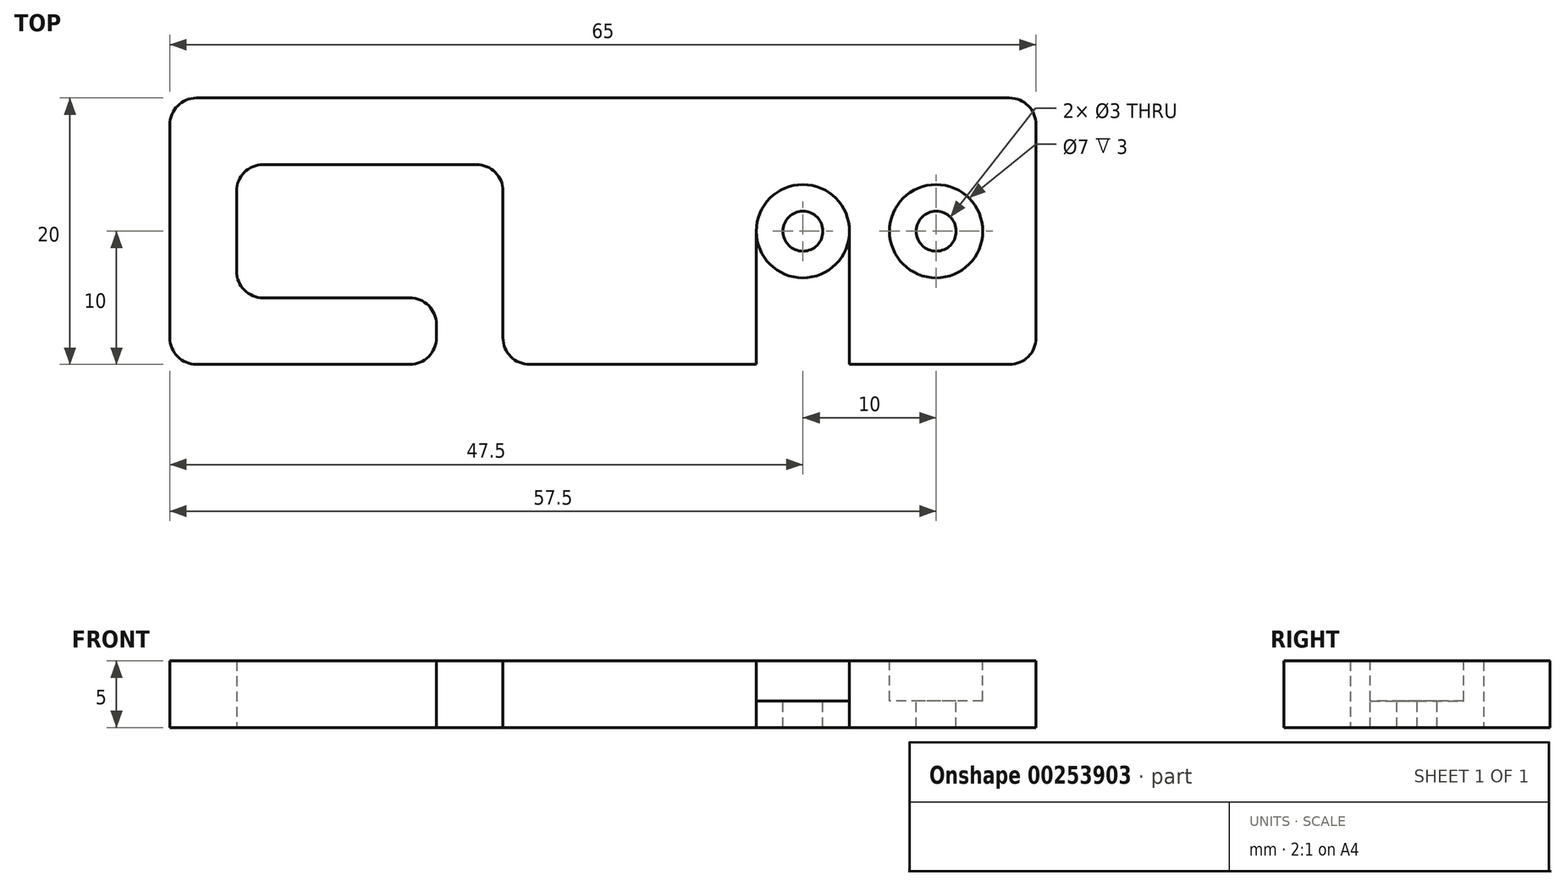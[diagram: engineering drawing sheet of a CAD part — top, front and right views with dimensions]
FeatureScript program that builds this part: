
annotation { "Feature Type Name" : "Feature", "Feature Type Description" : "" }
export const myFeature = defineFeature(function(context is Context, id is Id, definition is map)
    precondition{}
    {
        {
            var Q0;
            Q0=qCreatedBy(makeId("Top.planeOp"),FACE);
            var sketch = newSketch(context, id + "F0", { "sketchPlane" : qUnion([Q0])});
            skLineSegment(sketch, "E0.bottom", {"start": v(0, 0) * mm, "end": v(40, 0) * mm});
            skLineSegment(sketch, "E0.top", {"start": v(0, 20) * mm, "end": v(40, 20) * mm});
            skLineSegment(sketch, "E0.left", {"start": v(0, 0) * mm, "end": v(0, 15) * mm});
            skLineSegment(sketch, "E0.right", {"start": v(40, 0) * mm, "end": v(40, 20) * mm});
            skLineSegment(sketch, "E1.left", {"start": v(-20, 15) * mm, "end": v(-20, 5) * mm});
            skLineSegment(sketch, "E1.right", {"start": v(-25, 20) * mm, "end": v(-25, 0) * mm});
            skLineSegment(sketch, "E2.top", {"start": v(-20, 5) * mm, "end": v(-5, 5) * mm});
            skLineSegment(sketch, "E2.right", {"start": v(-5, 0) * mm, "end": v(-5, 5) * mm});
            skLineSegment(sketch, "E3", {"start": v(-25, 20) * mm, "end": v(0, 20) * mm});
            skLineSegment(sketch, "E4", {"start": v(-5, 0) * mm, "end": v(-25, 0) * mm});
            skLineSegment(sketch, "E5", {"start": v(-20, 15) * mm, "end": v(0, 15) * mm});
            skSolve(sketch);
        }
        {
            var Q0;
            Q0=makeQuery(id+"F0.imprint","IMPRINT",FACE,{"disambiguationData":[TD([[makeQuery(id+"F0.imprint","IMPRINT",EDGE,{"derivedFrom":sQuery(id+"F0.wireOp",EDGE,"E0.bottom")}),1.0]])]});
            extrude(context, id + "F1", {"entities" : qUnion([Q0]), "depth" : 5 * mm});
        }
        {
            var Q0;
            Q0=makeQuery(id+"F1.opExtrude","SWEPT_EDGE",EDGE,{"disambiguationData":[OSD([sQuery(id+"F0.wireOp",EDGE,"E1.right"),sQuery(id+"F0.wireOp",EDGE,"E4")])]});
            var Q1;
            Q1=makeQuery(id+"F1.opExtrude","SWEPT_EDGE",EDGE,{"disambiguationData":[OSD([sQuery(id+"F0.wireOp",EDGE,"E1.right"),sQuery(id+"F0.wireOp",EDGE,"E3")])]});
            var Q2;
            Q2=makeQuery(id+"F1.opExtrude","SWEPT_EDGE",EDGE,{"disambiguationData":[OSD([sQuery(id+"F0.wireOp",EDGE,"E0.bottom"),sQuery(id+"F0.wireOp",EDGE,"E0.right")])]});
            var Q3;
            Q3=makeQuery(id+"F1.opExtrude","SWEPT_EDGE",EDGE,{"disambiguationData":[OSD([sQuery(id+"F0.wireOp",EDGE,"E0.top"),sQuery(id+"F0.wireOp",EDGE,"E0.right")])]});
            var Q4;
            Q4=makeQuery(id+"F1.opExtrude","SWEPT_EDGE",EDGE,{"disambiguationData":[OSD([sQuery(id+"F0.wireOp",EDGE,"E0.bottom"),sQuery(id+"F0.wireOp",EDGE,"E0.left")])]});
            var Q5;
            Q5=makeQuery(id+"F1.opExtrude","SWEPT_EDGE",EDGE,{"disambiguationData":[OSD([sQuery(id+"F0.wireOp",EDGE,"E0.left"),sQuery(id+"F0.wireOp",EDGE,"E5")])]});
            var Q6;
            Q6=makeQuery(id+"F1.opExtrude","SWEPT_EDGE",EDGE,{"disambiguationData":[OSD([sQuery(id+"F0.wireOp",EDGE,"E2.right"),sQuery(id+"F0.wireOp",EDGE,"E4")])]});
            var Q7;
            Q7=makeQuery(id+"F1.opExtrude","SWEPT_EDGE",EDGE,{"disambiguationData":[OSD([sQuery(id+"F0.wireOp",EDGE,"E1.left"),sQuery(id+"F0.wireOp",EDGE,"E2.top")])]});
            var Q8;
            Q8=makeQuery(id+"F1.opExtrude","SWEPT_EDGE",EDGE,{"disambiguationData":[OSD([sQuery(id+"F0.wireOp",EDGE,"E2.top"),sQuery(id+"F0.wireOp",EDGE,"E2.right")])]});
            var Q9;
            Q9=makeQuery(id+"F1.opExtrude","SWEPT_EDGE",EDGE,{"disambiguationData":[OSD([sQuery(id+"F0.wireOp",EDGE,"E1.left"),sQuery(id+"F0.wireOp",EDGE,"E5")])]});
            fillet(context, id + "F2", {"entities" : qUnion([Q0, Q1, Q2, Q3, Q4, Q5, Q6, Q7, Q8, Q9]), "radius" : 2 * mm, "tangentPropagation" : true, "allowEdgeOverflow" : false});
        }
        {
            var Q0;
            Q0=makeQuery(id+"F1.opExtrude","CAP_FACE",FACE,{"disambiguationData":[OSD([sQuery(id+"F0.wireOp",EDGE,"E0.bottom"),sQuery(id+"F0.wireOp",EDGE,"E0.top"),sQuery(id+"F0.wireOp",EDGE,"E0.left"),sQuery(id+"F0.wireOp",EDGE,"E0.right"),sQuery(id+"F0.wireOp",EDGE,"E1.left"),sQuery(id+"F0.wireOp",EDGE,"E1.right"),sQuery(id+"F0.wireOp",EDGE,"E2.top"),sQuery(id+"F0.wireOp",EDGE,"E2.right"),sQuery(id+"F0.wireOp",EDGE,"E3"),sQuery(id+"F0.wireOp",EDGE,"E4"),sQuery(id+"F0.wireOp",EDGE,"E5")])],"isStart":false});
            var sketch = newSketch(context, id + "F3", { "sketchPlane" : qUnion([Q0])});
            skCircle(sketch, "E6", {"center": v(32.5, 10) * mm, "radius": 1.5 * mm});
            skCircle(sketch, "E7", {"center": v(32.5, 10) * mm, "radius": 3.5 * mm});
            skLineSegment(sketch, "E8", {"start": v(32.5, 10) * mm, "end": v(22.5, 10) * mm, "construction": true});
            skCircle(sketch, "E9", {"center": v(22.5, 10) * mm, "radius": 1.5 * mm});
            skCircle(sketch, "E10", {"center": v(22.5, 10) * mm, "radius": 3.5 * mm});
            skSolve(sketch);
        }
        {
            var Q0;
            Q0=makeQuery(id+"F3.imprint","IMPRINT",FACE,{"disambiguationData":[TD([[makeQuery(id+"F3.imprint","IMPRINT",EDGE,{"derivedFrom":sQuery(id+"F3.wireOp",EDGE,"E6")}),1.0]])]});
            var Q1;
            Q1=makeQuery(id+"F3.imprint","IMPRINT",FACE,{"disambiguationData":[TD([[makeQuery(id+"F3.imprint","IMPRINT",EDGE,{"derivedFrom":sQuery(id+"F3.wireOp",EDGE,"E9")}),1.0]])]});
            extrude(context, id + "F4", {"entities" : qUnion([Q0, Q1]), "operationType" : NewBodyOperationType.REMOVE, "endBound" : BoundingType.THROUGH_ALL, "oppositeDirection" : true, "depth" : 25 * mm});
        }
        {
            var Q0;
            Q0=makeQuery(id+"F3.imprint","IMPRINT",FACE,{"disambiguationData":[TD([[makeQuery(id+"F3.imprint","IMPRINT",EDGE,{"derivedFrom":sQuery(id+"F3.wireOp",EDGE,"E9")}),-1.0]])]});
            var Q1;
            Q1=makeQuery(id+"F3.imprint","IMPRINT",FACE,{"disambiguationData":[TD([[makeQuery(id+"F3.imprint","IMPRINT",EDGE,{"derivedFrom":sQuery(id+"F3.wireOp",EDGE,"E6")}),-1.0]])]});
            extrude(context, id + "F5", {"entities" : qUnion([Q0, Q1]), "operationType" : NewBodyOperationType.REMOVE, "oppositeDirection" : true, "depth" : 3 * mm});
        }
        {
            var Q0;
            Q0=makeQuery(id+"F1.opExtrude","CAP_FACE",FACE,{"disambiguationData":[OSD([sQuery(id+"F0.wireOp",EDGE,"E0.bottom"),sQuery(id+"F0.wireOp",EDGE,"E0.top"),sQuery(id+"F0.wireOp",EDGE,"E0.left"),sQuery(id+"F0.wireOp",EDGE,"E0.right"),sQuery(id+"F0.wireOp",EDGE,"E1.left"),sQuery(id+"F0.wireOp",EDGE,"E1.right"),sQuery(id+"F0.wireOp",EDGE,"E2.top"),sQuery(id+"F0.wireOp",EDGE,"E2.right"),sQuery(id+"F0.wireOp",EDGE,"E3"),sQuery(id+"F0.wireOp",EDGE,"E4"),sQuery(id+"F0.wireOp",EDGE,"E5")])],"isStart":false});
            var sketch = newSketch(context, id + "F6", { "sketchPlane" : qUnion([Q0])});
            skArc(sketch, "E11.0", {"start": v(19, 10) * mm, "mid": v(22.5, 6.5) * mm, "end": v(26, 10) * mm});
            skLineSegment(sketch, "E12.top", {"start": v(19, 0) * mm, "end": v(26, 0) * mm});
            skLineSegment(sketch, "E12.left", {"start": v(19, 10) * mm, "end": v(19, 0) * mm});
            skLineSegment(sketch, "E12.right", {"start": v(26, 10) * mm, "end": v(26, 0) * mm});
            skPoint(sketch, "E13.end.orphan", {"position": v(26, 10) * mm});
            skSolve(sketch);
        }
        {
            var Q0;
            Q0=makeQuery(id+"F6.imprint","IMPRINT",FACE,{"disambiguationData":[TD([[makeQuery(id+"F6.imprint","IMPRINT",EDGE,{"derivedFrom":sQuery(id+"F6.wireOp",EDGE,"E11.0")}),-1.0]])]});
            extrude(context, id + "F7", {"entities" : qUnion([Q0]), "operationType" : NewBodyOperationType.REMOVE, "endBound" : BoundingType.UP_TO_NEXT, "oppositeDirection" : true, "depth" : 25 * mm});
        }
    });
